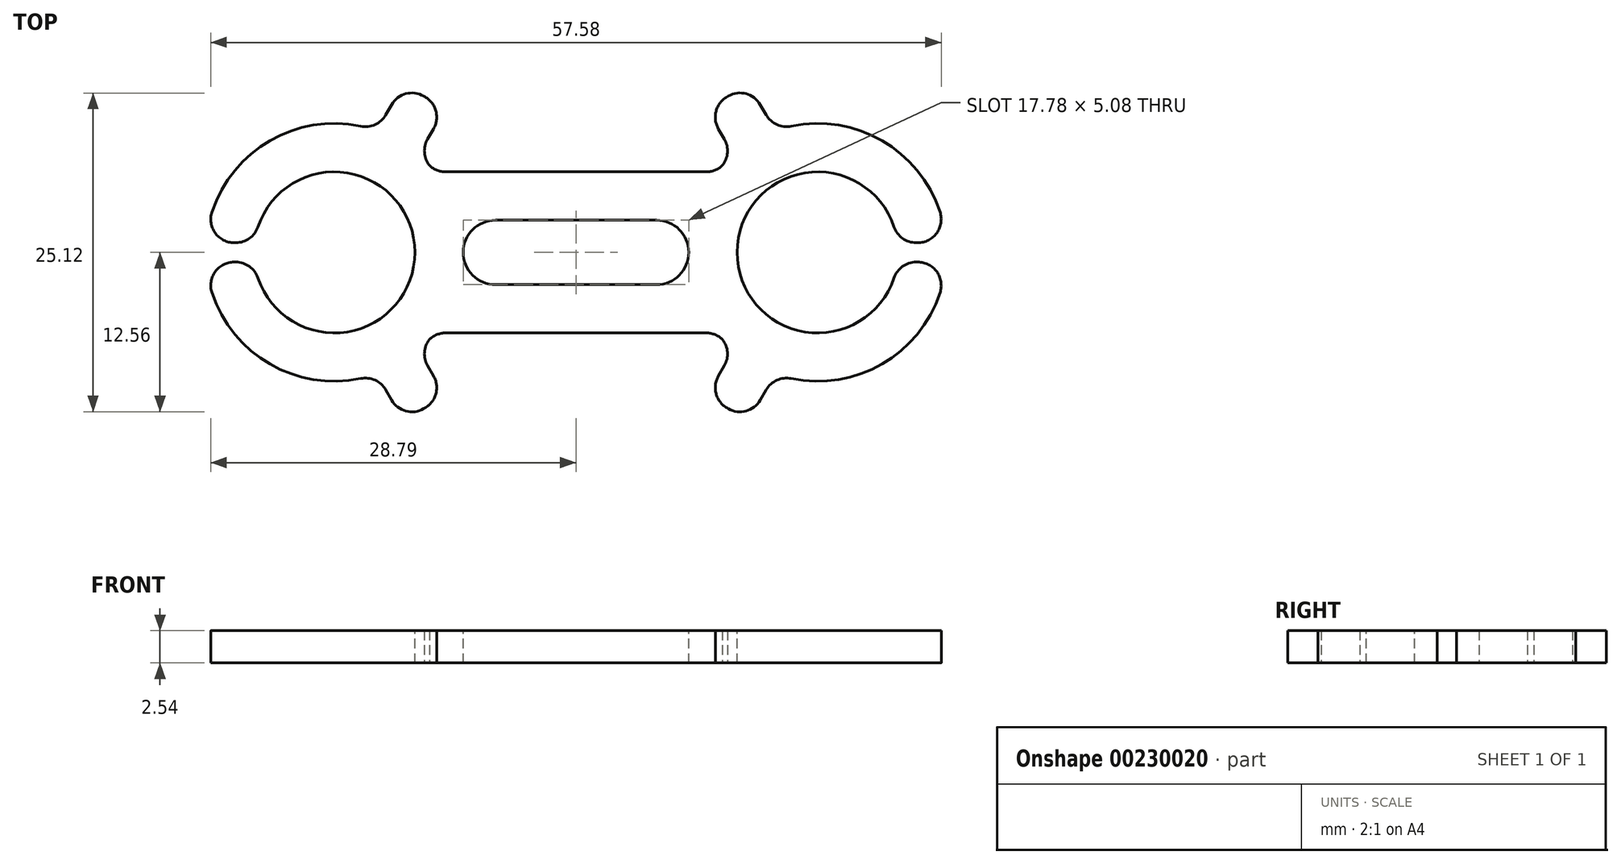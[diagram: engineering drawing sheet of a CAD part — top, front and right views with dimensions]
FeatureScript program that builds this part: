
annotation { "Feature Type Name" : "Feature", "Feature Type Description" : "" }
export const myFeature = defineFeature(function(context is Context, id is Id, definition is map)
    precondition{}
    {
        {
            var Q0;
            Q0=qCreatedBy(makeId("Top.planeOp"),FACE);
            var sketch = newSketch(context, id + "F0", { "sketchPlane" : qUnion([Q0])});
            skCircle(sketch, "E0", {"center": v(-19.05, 0) * mm, "radius": 10.16 * mm});
            skCircle(sketch, "E1", {"center": v(19.05, 0) * mm, "radius": 10.16 * mm});
            skLineSegment(sketch, "E2", {"start": v(-19.05, 0) * mm, "end": v(19.05, 0) * mm, "construction": true});
            skLineSegment(sketch, "E3", {"start": v(-19.05, 10.16) * mm, "end": v(19.05, 10.16) * mm, "construction": true});
            skLineSegment(sketch, "E4", {"start": v(19.05, -10.16) * mm, "end": v(-19.05, -10.16) * mm, "construction": true});
            skPoint(sketch, "E5", {"position": v(-13.97, 0) * mm});
            skPoint(sketch, "E6", {"position": v(-8.89, 0) * mm});
            skLineSegment(sketch, "E7.bottom", {"start": v(-11.12, 6.35) * mm, "end": v(11.12, 6.35) * mm});
            skLineSegment(sketch, "E7.top", {"start": v(-11.12, -6.35) * mm, "end": v(11.12, -6.35) * mm});
            skPoint(sketch, "E8", {"position": v(8.64, 0) * mm});
            skSolve(sketch);
        }
        {
            var Q0;
            Q0=qSketchRegion(id+"F0",true);
            extrude(context, id + "F1", {"entities" : qUnion([Q0]), "endBound" : BoundingType.SYMMETRIC, "depth" : 2.54 * mm});
        }
        {
            var Q0;
            Q0=makeQuery(id+"F1.opExtrude","CAP_FACE",FACE,{"disambiguationData":[OSD([sQuery(id+"F0.wireOp",EDGE,"E0"),sQuery(id+"F0.wireOp",EDGE,"E1"),sQuery(id+"F0.wireOp",EDGE,"JpsA0XJw-Zl1X-IY6a-TfOs-NOqodAkWJSI1")])],"isStart":false});
            var sketch = newSketch(context, id + "F2", { "sketchPlane" : qUnion([Q0])});
            skCircle(sketch, "E9", {"center": v(-19.05, 0) * mm, "radius": 6.35 * mm});
            skCircle(sketch, "E10", {"center": v(19.05, 0) * mm, "radius": 6.35 * mm});
            skSolve(sketch);
        }
        {
            var Q0;
            Q0=qSketchRegion(id+"F2",true);
            extrude(context, id + "F3", {"entities" : qUnion([Q0]), "operationType" : NewBodyOperationType.REMOVE, "oppositeDirection" : true, "depth" : 25.4 * mm});
        }
        {
            var Q0;
            Q0=makeQuery(id+"F1.opExtrude","CAP_FACE",FACE,{"disambiguationData":[OSD([sQuery(id+"F0.wireOp",EDGE,"E0"),sQuery(id+"F0.wireOp",EDGE,"E1"),sQuery(id+"F0.wireOp",EDGE,"JpsA0XJw-Zl1X-IY6a-TfOs-NOqodAkWJSI1")])],"isStart":false});
            var sketch = newSketch(context, id + "F4", { "sketchPlane" : qUnion([Q0])});
            skLineSegment(sketch, "E11", {"start": v(-19.05, 0) * mm, "end": v(-29.21, 0) * mm, "construction": true});
            skLineSegment(sketch, "E12.bottom", {"start": v(-29.21, 0.76) * mm, "end": v(-16.58, 0.76) * mm});
            skLineSegment(sketch, "E12.top", {"start": v(-29.21, -0.76) * mm, "end": v(-16.58, -0.76) * mm});
            skLineSegment(sketch, "E12.left", {"start": v(-29.21, 0.76) * mm, "end": v(-29.21, -0.76) * mm});
            skLineSegment(sketch, "E12.right", {"start": v(-16.58, 0.76) * mm, "end": v(-16.58, -0.76) * mm});
            skLineSegment(sketch, "E13", {"start": v(0, -0.63) * mm, "end": v(0, 19.69) * mm, "construction": true});
            skLineSegment(sketch, "E14.MirrorCS", {"start": v(16.58, 0.76) * mm, "end": v(16.58, -0.76) * mm});
            skLineSegment(sketch, "E15.MirrorCS", {"start": v(29.21, 0.76) * mm, "end": v(29.21, -0.76) * mm});
            skLineSegment(sketch, "E16.MirrorCS", {"start": v(19.05, 0) * mm, "end": v(29.21, 0) * mm, "construction": true});
            skLineSegment(sketch, "E17.MirrorCS", {"start": v(29.21, 0.76) * mm, "end": v(16.58, 0.76) * mm});
            skLineSegment(sketch, "E18.MirrorCS", {"start": v(29.21, -0.76) * mm, "end": v(16.58, -0.76) * mm});
            skSolve(sketch);
        }
        {
            var Q0;
            Q0=qSketchRegion(id+"F4",true);
            extrude(context, id + "F5", {"entities" : qUnion([Q0]), "operationType" : NewBodyOperationType.REMOVE, "oppositeDirection" : true, "depth" : 25.4 * mm});
        }
        {
            var Q0;
            Q0=makeQuery(id+"F1.opExtrude","CAP_FACE",FACE,{"disambiguationData":[OSD([sQuery(id+"F0.wireOp",EDGE,"E0"),sQuery(id+"F0.wireOp",EDGE,"E1"),sQuery(id+"F0.wireOp",EDGE,"E7.bottom"),sQuery(id+"F0.wireOp",EDGE,"E7.top")])],"isStart":false});
            var sketch = newSketch(context, id + "F6", { "sketchPlane" : qUnion([Q0])});
            skArc(sketch, "E19", {"start": v(-9.21, -2.54) * mm, "mid": v(-8.89, 0) * mm, "end": v(-9.21, 2.54) * mm});
            skArc(sketch, "E20", {"start": v(9.21, 2.54) * mm, "mid": v(8.89, 0) * mm, "end": v(9.21, -2.54) * mm});
            skLineSegment(sketch, "E21", {"start": v(-9.21, 2.54) * mm, "end": v(9.21, 2.54) * mm});
            skLineSegment(sketch, "E22", {"start": v(-9.21, -2.54) * mm, "end": v(9.21, -2.54) * mm});
            skSolve(sketch);
        }
        {
            var Q0;
            Q0=qSketchRegion(id+"F6",true);
            extrude(context, id + "F7", {"entities" : qUnion([Q0]), "operationType" : NewBodyOperationType.REMOVE, "oppositeDirection" : true, "depth" : 25.4 * mm});
        }
        {
            var Q0;
            Q0=makeQuery(id+"F7.boolean.opBoolean","COPY",EDGE,{"derivedFrom":makeQuery(id+"F7.opExtrude","SWEPT_EDGE",EDGE,{"disambiguationData":[OSD([sQuery(id+"F6.wireOp",EDGE,"E19"),sQuery(id+"F6.wireOp",EDGE,"E22")])]})});
            var Q1;
            Q1=makeQuery(id+"F7.boolean.opBoolean","COPY",EDGE,{"derivedFrom":makeQuery(id+"F7.opExtrude","SWEPT_EDGE",EDGE,{"disambiguationData":[OSD([sQuery(id+"F6.wireOp",EDGE,"E19"),sQuery(id+"F6.wireOp",EDGE,"E21")])]})});
            var Q2;
            Q2=makeQuery(id+"F7.boolean.opBoolean","COPY",EDGE,{"derivedFrom":makeQuery(id+"F7.opExtrude","SWEPT_EDGE",EDGE,{"disambiguationData":[OSD([sQuery(id+"F6.wireOp",EDGE,"E20"),sQuery(id+"F6.wireOp",EDGE,"E21")])]})});
            var Q3;
            Q3=makeQuery(id+"F7.boolean.opBoolean","COPY",EDGE,{"derivedFrom":makeQuery(id+"F7.opExtrude","SWEPT_EDGE",EDGE,{"disambiguationData":[OSD([sQuery(id+"F6.wireOp",EDGE,"E20"),sQuery(id+"F6.wireOp",EDGE,"E22")])]})});
            fillet(context, id + "F8", {"entities" : qUnion([Q0, Q1, Q2, Q3]), "radius" : 2.54 * mm, "tangentPropagation" : true, "allowEdgeOverflow" : false});
        }
        {
            var Q0;
            Q0=makeQuery(id+"F1.opExtrude","CAP_FACE",FACE,{"disambiguationData":[OSD([sQuery(id+"F0.wireOp",EDGE,"E0"),sQuery(id+"F0.wireOp",EDGE,"E1"),sQuery(id+"F0.wireOp",EDGE,"E7.bottom"),sQuery(id+"F0.wireOp",EDGE,"E7.top")])],"isStart":false});
            var sketch = newSketch(context, id + "F9", { "sketchPlane" : qUnion([Q0])});
            skLineSegment(sketch, "E23", {"start": v(-19.05, 0) * mm, "end": v(-11.96, 12.29) * mm, "construction": true});
            skLineSegment(sketch, "E24", {"start": v(-19.05, 0) * mm, "end": v(-19.05, 23.62) * mm, "construction": true});
            skLineSegment(sketch, "E25", {"start": v(-16.15, 8.84) * mm, "end": v(-13.6, 13.24) * mm});
            skLineSegment(sketch, "E26", {"start": v(-13.6, 13.24) * mm, "end": v(-10.3, 11.33) * mm});
            skLineSegment(sketch, "E27", {"start": v(-10.3, 11.33) * mm, "end": v(-12.85, 6.93) * mm});
            skLineSegment(sketch, "E28", {"start": v(-12.85, 6.93) * mm, "end": v(-16.15, 8.84) * mm});
            skLineSegment(sketch, "E29", {"start": v(-8.9, 0) * mm, "end": v(8.9, 0) * mm, "construction": true});
            skLineSegment(sketch, "E30", {"start": v(0, 6.35) * mm, "end": v(0, -6.35) * mm, "construction": true});
            skLineSegment(sketch, "E31.MirrorCS", {"start": v(12.85, 6.93) * mm, "end": v(16.15, 8.84) * mm});
            skLineSegment(sketch, "E32.MirrorCS", {"start": v(13.6, 13.24) * mm, "end": v(10.3, 11.33) * mm});
            skLineSegment(sketch, "E33.MirrorCS", {"start": v(16.15, 8.84) * mm, "end": v(13.6, 13.24) * mm});
            skLineSegment(sketch, "E34.MirrorCS", {"start": v(10.3, 11.33) * mm, "end": v(12.85, 6.93) * mm});
            skLineSegment(sketch, "E35.MirrorCS", {"start": v(-16.15, -8.84) * mm, "end": v(-13.6, -13.24) * mm});
            skLineSegment(sketch, "E36.MirrorCS", {"start": v(-12.85, -6.93) * mm, "end": v(-16.15, -8.84) * mm});
            skLineSegment(sketch, "E37.MirrorCS", {"start": v(-10.3, -11.33) * mm, "end": v(-12.85, -6.93) * mm});
            skLineSegment(sketch, "E38.MirrorCS", {"start": v(-13.6, -13.24) * mm, "end": v(-10.3, -11.33) * mm});
            skLineSegment(sketch, "E39.MirrorCS", {"start": v(10.3, -11.33) * mm, "end": v(12.85, -6.93) * mm});
            skLineSegment(sketch, "E40.MirrorCS", {"start": v(16.15, -8.84) * mm, "end": v(13.6, -13.24) * mm});
            skLineSegment(sketch, "E41.MirrorCS", {"start": v(13.6, -13.24) * mm, "end": v(10.3, -11.33) * mm});
            skLineSegment(sketch, "E42.MirrorCS", {"start": v(12.85, -6.93) * mm, "end": v(16.15, -8.84) * mm});
            skSolve(sketch);
        }
        {
            var Q0;
            Q0 = qSketchRegion(id + "F9", true);
            var Q1;
            Q1=makeQuery(id+"F1.opExtrude","CAP_FACE",FACE,{"disambiguationData":[OSD([sQuery(id+"F0.wireOp",EDGE,"E0"),sQuery(id+"F0.wireOp",EDGE,"E1"),sQuery(id+"F0.wireOp",EDGE,"E7.bottom"),sQuery(id+"F0.wireOp",EDGE,"E7.top")])],"isStart":true});
            extrude(context, id + "F10", {"entities" : qUnion([Q0]), "operationType" : NewBodyOperationType.ADD, "endBound" : BoundingType.UP_TO_SURFACE, "oppositeDirection" : true, "endBoundEntityFace" : qUnion([Q1]), "depth" : 25.4 * mm});
        }
        {
            var Q0;
            Q0=makeQuery(id+"F5.boolean.opBoolean","INTERSECT",EDGE,{"derivedFrom":[makeQuery(id+"F1.opExtrude","SWEPT_FACE",FACE,{"disambiguationData":[OSD([sQuery(id+"F0.wireOp",EDGE,"E0")])]}),makeQuery(id+"F5.opExtrude","SWEPT_FACE",FACE,{"disambiguationData":[OSD([sQuery(id+"F4.wireOp",EDGE,"E12.bottom")])]})]});
            var Q1;
            Q1=makeQuery(id+"F5.boolean.opBoolean","INTERSECT",EDGE,{"derivedFrom":[makeQuery(id+"F3.boolean.opBoolean","COPY",FACE,{"derivedFrom":makeQuery(id+"F3.opExtrude","SWEPT_FACE",FACE,{"disambiguationData":[OSD([sQuery(id+"F2.wireOp",EDGE,"E9")])]})}),makeQuery(id+"F5.opExtrude","SWEPT_FACE",FACE,{"disambiguationData":[OSD([sQuery(id+"F4.wireOp",EDGE,"E12.bottom")])]})]});
            var Q2;
            Q2=makeQuery(id+"F5.boolean.opBoolean","INTERSECT",EDGE,{"derivedFrom":[makeQuery(id+"F3.boolean.opBoolean","COPY",FACE,{"derivedFrom":makeQuery(id+"F3.opExtrude","SWEPT_FACE",FACE,{"disambiguationData":[OSD([sQuery(id+"F2.wireOp",EDGE,"E9")])]})}),makeQuery(id+"F5.opExtrude","SWEPT_FACE",FACE,{"disambiguationData":[OSD([sQuery(id+"F4.wireOp",EDGE,"E12.top")])]})]});
            var Q3;
            Q3=makeQuery(id+"F5.boolean.opBoolean","INTERSECT",EDGE,{"derivedFrom":[makeQuery(id+"F1.opExtrude","SWEPT_FACE",FACE,{"disambiguationData":[OSD([sQuery(id+"F0.wireOp",EDGE,"E0")])]}),makeQuery(id+"F5.opExtrude","SWEPT_FACE",FACE,{"disambiguationData":[OSD([sQuery(id+"F4.wireOp",EDGE,"E12.top")])]})]});
            var Q4;
            Q4=makeQuery(id+"F5.boolean.opBoolean","INTERSECT",EDGE,{"derivedFrom":[makeQuery(id+"F3.boolean.opBoolean","COPY",FACE,{"derivedFrom":makeQuery(id+"F3.opExtrude","SWEPT_FACE",FACE,{"disambiguationData":[OSD([sQuery(id+"F2.wireOp",EDGE,"E10")])]})}),makeQuery(id+"F5.opExtrude","SWEPT_FACE",FACE,{"disambiguationData":[OSD([sQuery(id+"F4.wireOp",EDGE,"E18.MirrorCS")])]})]});
            var Q5;
            Q5=makeQuery(id+"F5.boolean.opBoolean","INTERSECT",EDGE,{"derivedFrom":[makeQuery(id+"F3.boolean.opBoolean","COPY",FACE,{"derivedFrom":makeQuery(id+"F3.opExtrude","SWEPT_FACE",FACE,{"disambiguationData":[OSD([sQuery(id+"F2.wireOp",EDGE,"E10")])]})}),makeQuery(id+"F5.opExtrude","SWEPT_FACE",FACE,{"disambiguationData":[OSD([sQuery(id+"F4.wireOp",EDGE,"E17.MirrorCS")])]})]});
            var Q6;
            Q6=makeQuery(id+"F5.boolean.opBoolean","INTERSECT",EDGE,{"derivedFrom":[makeQuery(id+"F1.opExtrude","SWEPT_FACE",FACE,{"disambiguationData":[OSD([sQuery(id+"F0.wireOp",EDGE,"E1")])]}),makeQuery(id+"F5.opExtrude","SWEPT_FACE",FACE,{"disambiguationData":[OSD([sQuery(id+"F4.wireOp",EDGE,"E17.MirrorCS")])]})]});
            var Q7;
            Q7=makeQuery(id+"F5.boolean.opBoolean","INTERSECT",EDGE,{"derivedFrom":[makeQuery(id+"F1.opExtrude","SWEPT_FACE",FACE,{"disambiguationData":[OSD([sQuery(id+"F0.wireOp",EDGE,"E1")])]}),makeQuery(id+"F5.opExtrude","SWEPT_FACE",FACE,{"disambiguationData":[OSD([sQuery(id+"F4.wireOp",EDGE,"E18.MirrorCS")])]})]});
            var Q8;
            Q8=makeQuery(id+"F1.opExtrude","SWEPT_EDGE",EDGE,{"disambiguationData":[OSD([sQuery(id+"F0.wireOp",EDGE,"E0"),sQuery(id+"F0.wireOp",EDGE,"E7.top")])]});
            var Q9;
            Q9=makeQuery(id+"F1.opExtrude","SWEPT_EDGE",EDGE,{"disambiguationData":[OSD([sQuery(id+"F0.wireOp",EDGE,"E1"),sQuery(id+"F0.wireOp",EDGE,"E7.top")])]});
            var Q10;
            Q10=makeQuery(id+"F1.opExtrude","SWEPT_EDGE",EDGE,{"disambiguationData":[OSD([sQuery(id+"F0.wireOp",EDGE,"E1"),sQuery(id+"F0.wireOp",EDGE,"E7.bottom")])]});
            var Q11;
            Q11=makeQuery(id+"F1.opExtrude","SWEPT_EDGE",EDGE,{"disambiguationData":[OSD([sQuery(id+"F0.wireOp",EDGE,"E0"),sQuery(id+"F0.wireOp",EDGE,"E7.bottom")])]});
            var Q12;
            Q12=makeQuery(id+"F10.opExtrude","SWEPT_EDGE",EDGE,{"disambiguationData":[OSD([sQuery(id+"F9.wireOp",EDGE,"E37.MirrorCS"),sQuery(id+"F9.wireOp",EDGE,"E38.MirrorCS")])]});
            var Q13;
            Q13=makeQuery(id+"F10.opExtrude","SWEPT_EDGE",EDGE,{"disambiguationData":[OSD([sQuery(id+"F9.wireOp",EDGE,"E35.MirrorCS"),sQuery(id+"F9.wireOp",EDGE,"E38.MirrorCS")])]});
            var Q14;
            Q14=makeQuery(id+"F10.opExtrude","SWEPT_EDGE",EDGE,{"disambiguationData":[OSD([sQuery(id+"F9.wireOp",EDGE,"E39.MirrorCS"),sQuery(id+"F9.wireOp",EDGE,"E41.MirrorCS")])]});
            var Q15;
            Q15=makeQuery(id+"F10.opExtrude","SWEPT_EDGE",EDGE,{"disambiguationData":[OSD([sQuery(id+"F9.wireOp",EDGE,"E40.MirrorCS"),sQuery(id+"F9.wireOp",EDGE,"E41.MirrorCS")])]});
            var Q16;
            Q16=makeQuery(id+"F10.opExtrude","SWEPT_EDGE",EDGE,{"disambiguationData":[OSD([sQuery(id+"F9.wireOp",EDGE,"E32.MirrorCS"),sQuery(id+"F9.wireOp",EDGE,"E33.MirrorCS")])]});
            var Q17;
            Q17=makeQuery(id+"F10.opExtrude","SWEPT_EDGE",EDGE,{"disambiguationData":[OSD([sQuery(id+"F9.wireOp",EDGE,"E32.MirrorCS"),sQuery(id+"F9.wireOp",EDGE,"E34.MirrorCS")])]});
            var Q18;
            Q18=makeQuery(id+"F10.opExtrude","SWEPT_EDGE",EDGE,{"disambiguationData":[OSD([sQuery(id+"F9.wireOp",EDGE,"E26"),sQuery(id+"F9.wireOp",EDGE,"E27")])]});
            var Q19;
            Q19=makeQuery(id+"F10.opExtrude","SWEPT_EDGE",EDGE,{"disambiguationData":[OSD([sQuery(id+"F9.wireOp",EDGE,"E25"),sQuery(id+"F9.wireOp",EDGE,"E26")])]});
            var Q20;
            {var subQ1=sQuery(id+"F0.wireOp",EDGE,"E7.bottom");var subQ3=sQuery(id+"F0.wireOp",EDGE,"E0");Q20=makeQuery(id+"F10.boolean.opBoolean","INTERSECT",EDGE,{"derivedFrom":[makeQuery(id+"F5.boolean.opBoolean","SPLIT",FACE,{"disambiguationData":[TD([makeQuery(id+"F1.opExtrude","SWEPT_FACE",FACE,{"disambiguationData":[OSD([subQ1])]})])],"derivedFrom":makeQuery(id+"F1.opExtrude","SWEPT_FACE",FACE,{"disambiguationData":[OSD([subQ3])]})}),makeQuery(id+"F10.opExtrude","SWEPT_FACE",FACE,{"disambiguationData":[OSD([sQuery(id+"F9.wireOp",EDGE,"E25")])]})]});}
            var Q21;
            {var subQ0=sQuery(id+"F0.wireOp",EDGE,"E7.top");var subQ3=sQuery(id+"F0.wireOp",EDGE,"E0");Q21=makeQuery(id+"F10.boolean.opBoolean","INTERSECT",EDGE,{"derivedFrom":[makeQuery(id+"F5.boolean.opBoolean","SPLIT",FACE,{"disambiguationData":[TD([makeQuery(id+"F1.opExtrude","SWEPT_FACE",FACE,{"disambiguationData":[OSD([subQ0])]})])],"derivedFrom":makeQuery(id+"F1.opExtrude","SWEPT_FACE",FACE,{"disambiguationData":[OSD([subQ3])]})}),makeQuery(id+"F10.opExtrude","SWEPT_FACE",FACE,{"disambiguationData":[OSD([sQuery(id+"F9.wireOp",EDGE,"E35.MirrorCS")])]})]});}
            var Q22;
            {var subQ0=sQuery(id+"F0.wireOp",EDGE,"E7.top");var subQ3=sQuery(id+"F0.wireOp",EDGE,"E0");Q22=makeQuery(id+"F10.boolean.opBoolean","INTERSECT",EDGE,{"derivedFrom":[makeQuery(id+"F5.boolean.opBoolean","SPLIT",FACE,{"disambiguationData":[TD([makeQuery(id+"F1.opExtrude","SWEPT_FACE",FACE,{"disambiguationData":[OSD([subQ0])]})])],"derivedFrom":makeQuery(id+"F1.opExtrude","SWEPT_FACE",FACE,{"disambiguationData":[OSD([subQ3])]})}),makeQuery(id+"F10.opExtrude","SWEPT_FACE",FACE,{"disambiguationData":[OSD([sQuery(id+"F9.wireOp",EDGE,"E37.MirrorCS")])]})]});}
            var Q23;
            {var subQ0=sQuery(id+"F0.wireOp",EDGE,"E7.top");var subQ2=sQuery(id+"F0.wireOp",EDGE,"E1");Q23=makeQuery(id+"F10.boolean.opBoolean","INTERSECT",EDGE,{"derivedFrom":[makeQuery(id+"F5.boolean.opBoolean","SPLIT",FACE,{"disambiguationData":[TD([makeQuery(id+"F1.opExtrude","SWEPT_FACE",FACE,{"disambiguationData":[OSD([subQ0])]})])],"derivedFrom":makeQuery(id+"F1.opExtrude","SWEPT_FACE",FACE,{"disambiguationData":[OSD([subQ2])]})}),makeQuery(id+"F10.opExtrude","SWEPT_FACE",FACE,{"disambiguationData":[OSD([sQuery(id+"F9.wireOp",EDGE,"E39.MirrorCS")])]})]});}
            var Q24;
            {var subQ0=sQuery(id+"F0.wireOp",EDGE,"E7.top");var subQ2=sQuery(id+"F0.wireOp",EDGE,"E1");Q24=makeQuery(id+"F10.boolean.opBoolean","INTERSECT",EDGE,{"derivedFrom":[makeQuery(id+"F5.boolean.opBoolean","SPLIT",FACE,{"disambiguationData":[TD([makeQuery(id+"F1.opExtrude","SWEPT_FACE",FACE,{"disambiguationData":[OSD([subQ0])]})])],"derivedFrom":makeQuery(id+"F1.opExtrude","SWEPT_FACE",FACE,{"disambiguationData":[OSD([subQ2])]})}),makeQuery(id+"F10.opExtrude","SWEPT_FACE",FACE,{"disambiguationData":[OSD([sQuery(id+"F9.wireOp",EDGE,"E40.MirrorCS")])]})]});}
            var Q25;
            {var subQ1=sQuery(id+"F0.wireOp",EDGE,"E7.bottom");var subQ2=sQuery(id+"F0.wireOp",EDGE,"E1");Q25=makeQuery(id+"F10.boolean.opBoolean","INTERSECT",EDGE,{"derivedFrom":[makeQuery(id+"F5.boolean.opBoolean","SPLIT",FACE,{"disambiguationData":[TD([makeQuery(id+"F1.opExtrude","SWEPT_FACE",FACE,{"disambiguationData":[OSD([subQ1])]})])],"derivedFrom":makeQuery(id+"F1.opExtrude","SWEPT_FACE",FACE,{"disambiguationData":[OSD([subQ2])]})}),makeQuery(id+"F10.opExtrude","SWEPT_FACE",FACE,{"disambiguationData":[OSD([sQuery(id+"F9.wireOp",EDGE,"E34.MirrorCS")])]})]});}
            var Q26;
            {var subQ1=sQuery(id+"F0.wireOp",EDGE,"E7.bottom");var subQ2=sQuery(id+"F0.wireOp",EDGE,"E1");Q26=makeQuery(id+"F10.boolean.opBoolean","INTERSECT",EDGE,{"derivedFrom":[makeQuery(id+"F5.boolean.opBoolean","SPLIT",FACE,{"disambiguationData":[TD([makeQuery(id+"F1.opExtrude","SWEPT_FACE",FACE,{"disambiguationData":[OSD([subQ1])]})])],"derivedFrom":makeQuery(id+"F1.opExtrude","SWEPT_FACE",FACE,{"disambiguationData":[OSD([subQ2])]})}),makeQuery(id+"F10.opExtrude","SWEPT_FACE",FACE,{"disambiguationData":[OSD([sQuery(id+"F9.wireOp",EDGE,"E33.MirrorCS")])]})]});}
            var Q27;
            {var subQ1=sQuery(id+"F0.wireOp",EDGE,"E7.bottom");var subQ3=sQuery(id+"F0.wireOp",EDGE,"E0");Q27=makeQuery(id+"F10.boolean.opBoolean","INTERSECT",EDGE,{"derivedFrom":[makeQuery(id+"F5.boolean.opBoolean","SPLIT",FACE,{"disambiguationData":[TD([makeQuery(id+"F1.opExtrude","SWEPT_FACE",FACE,{"disambiguationData":[OSD([subQ1])]})])],"derivedFrom":makeQuery(id+"F1.opExtrude","SWEPT_FACE",FACE,{"disambiguationData":[OSD([subQ3])]})}),makeQuery(id+"F10.opExtrude","SWEPT_FACE",FACE,{"disambiguationData":[OSD([sQuery(id+"F9.wireOp",EDGE,"E27")])]})]});}
            fillet(context, id + "F11", {"entities" : qUnion([Q0, Q1, Q2, Q3, Q4, Q5, Q6, Q7, Q8, Q9, Q10, Q11, Q12, Q13, Q14, Q15, Q16, Q17, Q18, Q19, Q20, Q21, Q22, Q23, Q24, Q25, Q26, Q27]), "radius" : 1.84 * mm, "tangentPropagation" : true, "allowEdgeOverflow" : false});
        }
    });
